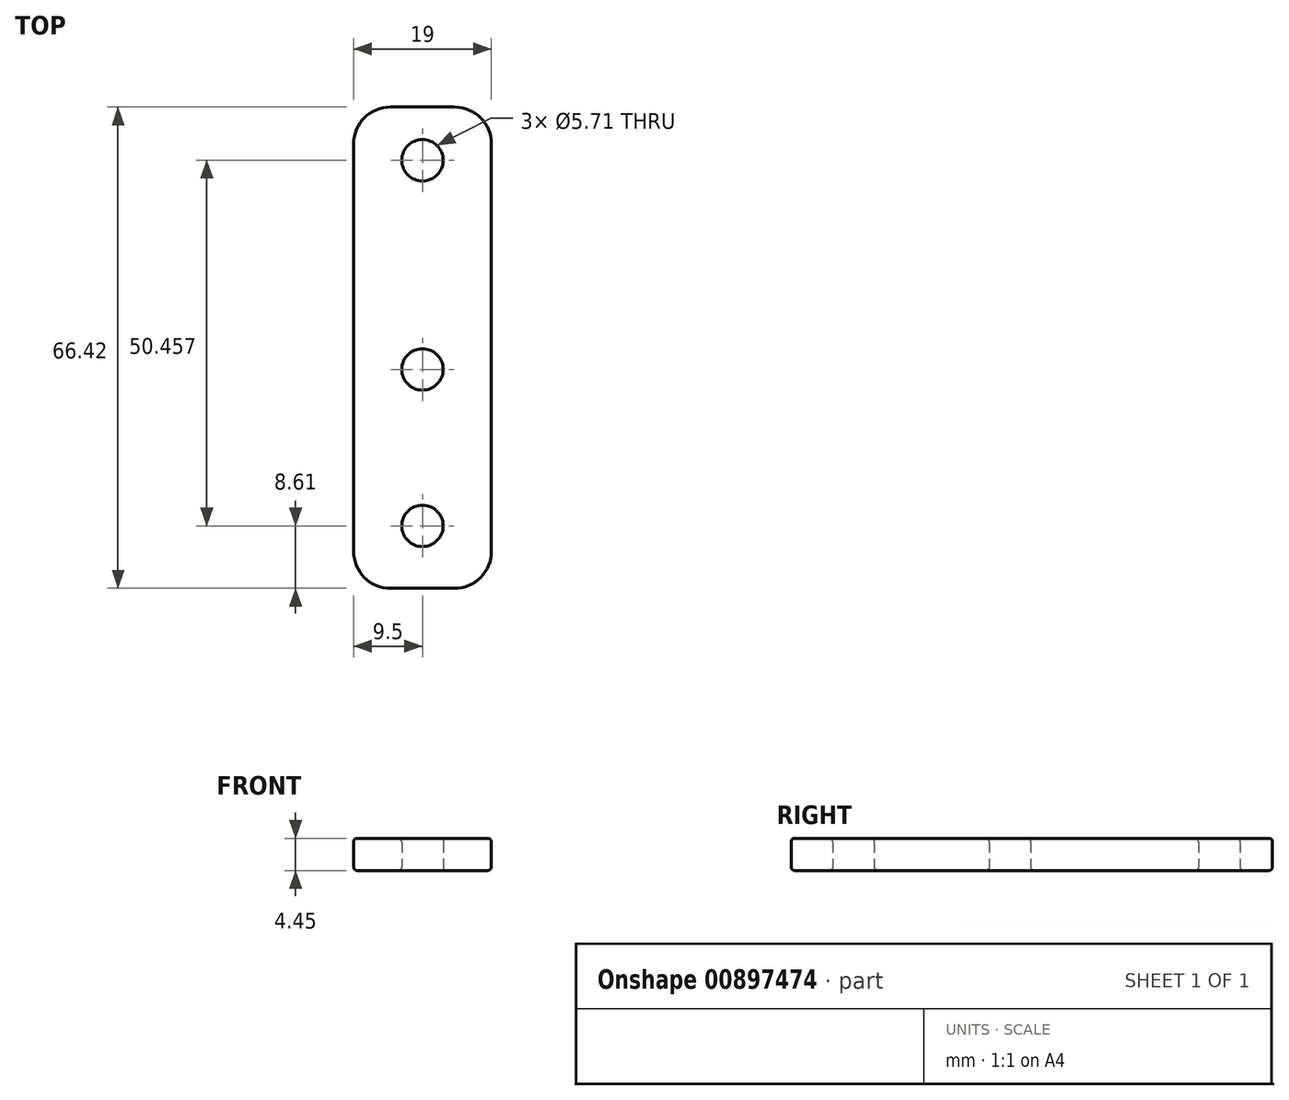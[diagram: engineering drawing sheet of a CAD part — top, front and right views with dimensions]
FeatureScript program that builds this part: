
annotation { "Feature Type Name" : "Feature", "Feature Type Description" : "" }
export const myFeature = defineFeature(function(context is Context, id is Id, definition is map)
    precondition{}
    {
        {
            var Q0;
            Q0=qCreatedBy(makeId("Top.planeOp"),FACE);
            var sketch = newSketch(context, id + "F0", { "sketchPlane" : qUnion([Q0])});
            skLineSegment(sketch, "E0", {"start": v(0, 0) * mm, "end": v(0, 45.72) * mm});
            skLineSegment(sketch, "E1", {"start": v(0, 45.72) * mm, "end": v(-19, 45.72) * mm});
            skLineSegment(sketch, "E2", {"start": v(-19, 45.72) * mm, "end": v(-19, 19) * mm});
            skLineSegment(sketch, "E3", {"start": v(-19, 19) * mm, "end": v(-19, 19) * mm});
            skLineSegment(sketch, "E4", {"start": v(-19, 19) * mm, "end": v(-19, 0) * mm});
            skLineSegment(sketch, "E5", {"start": v(-19, 0) * mm, "end": v(0, 0) * mm});
            skCircle(sketch, "E6", {"center": v(-9.5, 38.37) * mm, "radius": 2.86 * mm});
            skLineSegment(sketch, "E7", {"start": v(-9.5, 45.72) * mm, "end": v(-9.5, 0) * mm, "construction": true});
            skCircle(sketch, "E8", {"center": v(-9.5, 9.5) * mm, "radius": 2.86 * mm});
            skLineSegment(sketch, "E9.top", {"start": v(-19, -20.7) * mm, "end": v(0, -20.7) * mm});
            skLineSegment(sketch, "E9.left", {"start": v(-19, 0) * mm, "end": v(-19, -20.7) * mm});
            skLineSegment(sketch, "E9.right", {"start": v(0, 0) * mm, "end": v(0, -20.7) * mm});
            skLineSegment(sketch, "E10", {"start": v(-9.5, 0) * mm, "end": v(-9.5, -20.7) * mm, "construction": true});
            skCircle(sketch, "E11", {"center": v(-9.5, -12.09) * mm, "radius": 2.86 * mm});
            skLineSegment(sketch, "E12", {"start": v(-19, 9.5) * mm, "end": v(-9.5, 9.5) * mm, "construction": true});
            skSolve(sketch);
        }
        {
            var Q0;
            Q0=makeQuery(id+"F0.imprint","IMPRINT",FACE,{"disambiguationData":[TD([[makeQuery(id+"F0.imprint","IMPRINT",EDGE,{"derivedFrom":sQuery(id+"F0.wireOp",EDGE,"E0")}),1.0]])]});
            var Q1;
            Q1=makeQuery(id+"F0.imprint","IMPRINT",FACE,{"disambiguationData":[TD([[makeQuery(id+"F0.imprint","IMPRINT",EDGE,{"derivedFrom":sQuery(id+"F0.wireOp",EDGE,"E5")}),-1.0]])]});
            extrude(context, id + "F1", {"entities" : qUnion([Q0, Q1]), "depth" : 4.44 * mm, "offsetDistance" : 25.4 * mm});
        }
        {
            var Q0;
            Q0=makeQuery(id+"F1.opExtrude","SWEPT_EDGE",EDGE,{"disambiguationData":[OSD([sQuery(id+"F0.wireOp",EDGE,"E0"),sQuery(id+"F0.wireOp",EDGE,"E5")])]});
            var Q1;
            Q1=makeQuery(id+"F1.opExtrude","SWEPT_EDGE",EDGE,{"disambiguationData":[OSD([sQuery(id+"F0.wireOp",EDGE,"E4"),sQuery(id+"F0.wireOp",EDGE,"E5")])]});
            var Q2;
            Q2=makeQuery(id+"F1.opExtrude","SWEPT_EDGE",EDGE,{"disambiguationData":[OSD([sQuery(id+"F0.wireOp",EDGE,"E3"),sQuery(id+"F0.wireOp",EDGE,"E4")])]});
            var Q3;
            Q3=makeQuery(id+"F1.opExtrude","SWEPT_EDGE",EDGE,{"disambiguationData":[OSD([sQuery(id+"F0.wireOp",EDGE,"E2"),sQuery(id+"F0.wireOp",EDGE,"E3")])]});
            var Q4;
            Q4=makeQuery(id+"F1.opExtrude","SWEPT_EDGE",EDGE,{"disambiguationData":[OSD([sQuery(id+"F0.wireOp",EDGE,"E1"),sQuery(id+"F0.wireOp",EDGE,"E2")])]});
            var Q5;
            Q5=makeQuery(id+"F1.opExtrude","SWEPT_EDGE",EDGE,{"disambiguationData":[OSD([sQuery(id+"F0.wireOp",EDGE,"E0"),sQuery(id+"F0.wireOp",EDGE,"E1")])]});
            var Q6;
            Q6=makeQuery(id+"F1.opExtrude","SWEPT_EDGE",EDGE,{"disambiguationData":[OSD([sQuery(id+"F0.wireOp",EDGE,"E9.top"),sQuery(id+"F0.wireOp",EDGE,"E9.right")])]});
            var Q7;
            Q7=makeQuery(id+"F1.opExtrude","SWEPT_EDGE",EDGE,{"disambiguationData":[OSD([sQuery(id+"F0.wireOp",EDGE,"E9.top"),sQuery(id+"F0.wireOp",EDGE,"E9.left")])]});
            fillet(context, id + "F2", {"entities" : qUnion([Q0, Q1, Q2, Q3, Q4, Q5, Q6, Q7]), "radius" : 5.08 * mm, "tangentPropagation" : true, "allowEdgeOverflow" : false});
        }
        {
            var Q0;
            Q0=makeQuery(id+"F1.opExtrude","CAP_EDGE",EDGE,{"disambiguationData":[OSD([sQuery(id+"F0.wireOp",EDGE,"E0")])],"isStart":false});
            var Q1;
            Q1=makeQuery(id+"F1.opExtrude","CAP_EDGE",EDGE,{"disambiguationData":[OSD([sQuery(id+"F0.wireOp",EDGE,"E8")])],"isStart":false});
            var Q2;
            Q2=makeQuery(id+"F1.opExtrude","CAP_EDGE",EDGE,{"disambiguationData":[OSD([sQuery(id+"F0.wireOp",EDGE,"NaQKEjHk-Z6LA-96tM-WqRa-bFAFSZEO5QkA")])],"isStart":false});
            var Q3;
            Q3=makeQuery(id+"F1.opExtrude","CAP_EDGE",EDGE,{"disambiguationData":[OSD([sQuery(id+"F0.wireOp",EDGE,"E6")])],"isStart":false});
            var Q4;
            Q4=makeQuery(id+"F1.opExtrude","CAP_EDGE",EDGE,{"disambiguationData":[OSD([sQuery(id+"F0.wireOp",EDGE,"E0")])],"isStart":true});
            var Q5;
            Q5=makeQuery(id+"F1.opExtrude","CAP_EDGE",EDGE,{"disambiguationData":[OSD([sQuery(id+"F0.wireOp",EDGE,"E8")])],"isStart":true});
            var Q6;
            Q6=makeQuery(id+"F1.opExtrude","CAP_EDGE",EDGE,{"disambiguationData":[OSD([sQuery(id+"F0.wireOp",EDGE,"NaQKEjHk-Z6LA-96tM-WqRa-bFAFSZEO5QkA")])],"isStart":true});
            var Q7;
            Q7=makeQuery(id+"F1.opExtrude","CAP_EDGE",EDGE,{"disambiguationData":[OSD([sQuery(id+"F0.wireOp",EDGE,"E11")])],"isStart":false});
            var Q8;
            Q8=makeQuery(id+"F1.opExtrude","CAP_EDGE",EDGE,{"disambiguationData":[OSD([sQuery(id+"F0.wireOp",EDGE,"E11")])],"isStart":true});
            var Q9;
            Q9=makeQuery(id+"F1.opExtrude","CAP_EDGE",EDGE,{"disambiguationData":[OSD([sQuery(id+"F0.wireOp",EDGE,"E6")])],"isStart":true});
            fillet(context, id + "F3", {"entities" : qUnion([Q0, Q1, Q2, Q3, Q4, Q5, Q6, Q7, Q8, Q9]), "radius" : 0.5 * mm, "tangentPropagation" : true, "allowEdgeOverflow" : false});
        }
    });
